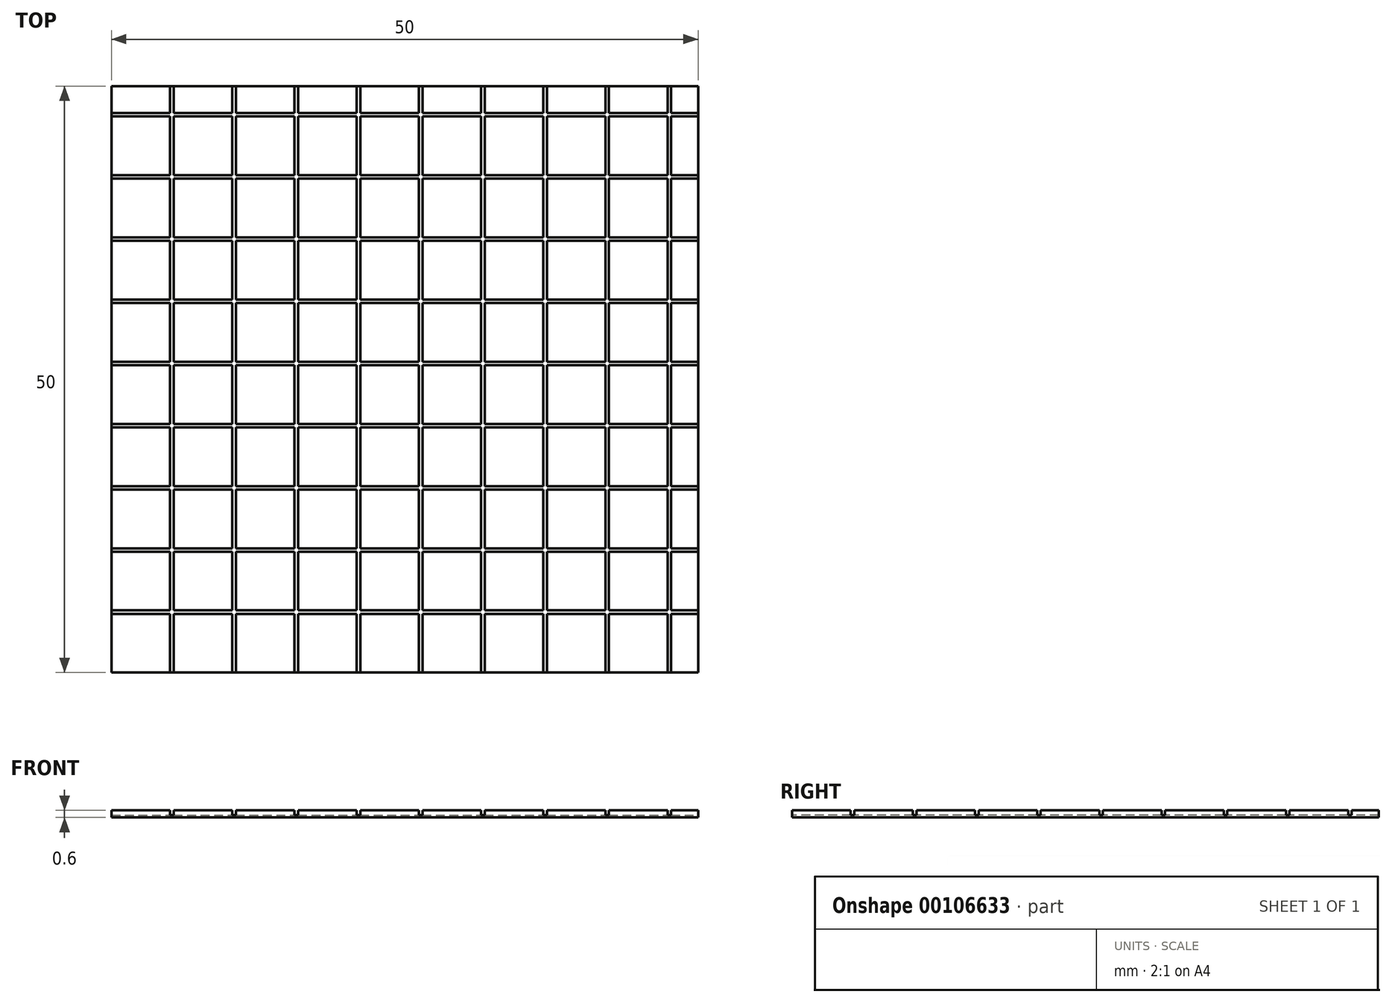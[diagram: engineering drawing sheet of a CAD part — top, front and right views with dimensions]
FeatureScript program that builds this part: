
annotation { "Feature Type Name" : "Feature", "Feature Type Description" : "" }
export const myFeature = defineFeature(function(context is Context, id is Id, definition is map)
    precondition{}
    {
        {
            var Q0;
            Q0=qCreatedBy(makeId("Top.planeOp"),FACE);
            var sketch = newSketch(context, id + "F0", { "sketchPlane" : qUnion([Q0])});
            skLineSegment(sketch, "E0.bottom", {"start": v(0, 0) * mm, "end": v(50, 0) * mm});
            skLineSegment(sketch, "E0.top", {"start": v(0, 50) * mm, "end": v(50, 50) * mm});
            skLineSegment(sketch, "E0.left", {"start": v(0, 0) * mm, "end": v(0, 50) * mm});
            skLineSegment(sketch, "E0.right", {"start": v(50, 0) * mm, "end": v(50, 50) * mm});
            skSolve(sketch);
        }
        {
            var Q0;
            Q0 = qSketchRegion(id + "F0", true);
            extrude(context, id + "F1", {"entities" : qUnion([Q0]), "depth" : 0.6 * mm});
        }
        {
            var Q0;
            Q0=makeQuery(id+"F1.opExtrude","CAP_FACE",FACE,{"disambiguationData":[OSD([sQuery(id+"F0.wireOp",EDGE,"E0.bottom"),sQuery(id+"F0.wireOp",EDGE,"E0.top"),sQuery(id+"F0.wireOp",EDGE,"E0.left"),sQuery(id+"F0.wireOp",EDGE,"E0.right")])],"isStart":false});
            var sketch = newSketch(context, id + "F2", { "sketchPlane" : qUnion([Q0])});
            skLineSegment(sketch, "E1.bottom", {"start": v(5, 50) * mm, "end": v(5.3, 50) * mm});
            skLineSegment(sketch, "E1.top", {"start": v(5, 0) * mm, "end": v(5.3, 0) * mm});
            skLineSegment(sketch, "E1.left", {"start": v(5, 50) * mm, "end": v(5, 0) * mm});
            skLineSegment(sketch, "E1.right", {"start": v(5.3, 50) * mm, "end": v(5.3, 0) * mm});
            skLineSegment(sketch, "E2.1.0.0", {"start": v(10.3, 50) * mm, "end": v(10.3, 0) * mm});
            skLineSegment(sketch, "E2.1.0.1", {"start": v(10.6, 50) * mm, "end": v(10.6, 0) * mm});
            skLineSegment(sketch, "E2.1.0.2", {"start": v(10.3, 0) * mm, "end": v(10.6, 0) * mm});
            skLineSegment(sketch, "E2.1.0.3", {"start": v(10.3, 50) * mm, "end": v(10.6, 50) * mm});
            skLineSegment(sketch, "E2.2.0.0", {"start": v(15.6, 50) * mm, "end": v(15.6, 0) * mm});
            skLineSegment(sketch, "E2.2.0.1", {"start": v(15.9, 50) * mm, "end": v(15.9, 0) * mm});
            skLineSegment(sketch, "E2.2.0.2", {"start": v(15.6, 0) * mm, "end": v(15.9, 0) * mm});
            skLineSegment(sketch, "E2.2.0.3", {"start": v(15.6, 50) * mm, "end": v(15.9, 50) * mm});
            skLineSegment(sketch, "E2.3.0.0", {"start": v(20.9, 50) * mm, "end": v(20.9, 0) * mm});
            skLineSegment(sketch, "E2.3.0.1", {"start": v(21.2, 50) * mm, "end": v(21.2, 0) * mm});
            skLineSegment(sketch, "E2.3.0.2", {"start": v(20.9, 0) * mm, "end": v(21.2, 0) * mm});
            skLineSegment(sketch, "E2.3.0.3", {"start": v(20.9, 50) * mm, "end": v(21.2, 50) * mm});
            skLineSegment(sketch, "E2.4.0.0", {"start": v(26.2, 50) * mm, "end": v(26.2, 0) * mm});
            skLineSegment(sketch, "E2.4.0.1", {"start": v(26.5, 50) * mm, "end": v(26.5, 0) * mm});
            skLineSegment(sketch, "E2.4.0.2", {"start": v(26.2, 0) * mm, "end": v(26.5, 0) * mm});
            skLineSegment(sketch, "E2.4.0.3", {"start": v(26.2, 50) * mm, "end": v(26.5, 50) * mm});
            skLineSegment(sketch, "E2.5.0.0", {"start": v(31.5, 50) * mm, "end": v(31.5, 0) * mm});
            skLineSegment(sketch, "E2.5.0.1", {"start": v(31.8, 50) * mm, "end": v(31.8, 0) * mm});
            skLineSegment(sketch, "E2.5.0.2", {"start": v(31.5, 0) * mm, "end": v(31.8, 0) * mm});
            skLineSegment(sketch, "E2.5.0.3", {"start": v(31.5, 50) * mm, "end": v(31.8, 50) * mm});
            skLineSegment(sketch, "E2.6.0.0", {"start": v(36.8, 50) * mm, "end": v(36.8, 0) * mm});
            skLineSegment(sketch, "E2.6.0.1", {"start": v(37.1, 50) * mm, "end": v(37.1, 0) * mm});
            skLineSegment(sketch, "E2.6.0.2", {"start": v(36.8, 0) * mm, "end": v(37.1, 0) * mm});
            skLineSegment(sketch, "E2.6.0.3", {"start": v(36.8, 50) * mm, "end": v(37.1, 50) * mm});
            skLineSegment(sketch, "E2.7.0.0", {"start": v(42.1, 50) * mm, "end": v(42.1, 0) * mm});
            skLineSegment(sketch, "E2.7.0.1", {"start": v(42.4, 50) * mm, "end": v(42.4, 0) * mm});
            skLineSegment(sketch, "E2.7.0.2", {"start": v(42.1, 0) * mm, "end": v(42.4, 0) * mm});
            skLineSegment(sketch, "E2.7.0.3", {"start": v(42.1, 50) * mm, "end": v(42.4, 50) * mm});
            skLineSegment(sketch, "E2.8.0.0", {"start": v(47.4, 50) * mm, "end": v(47.4, 0) * mm});
            skLineSegment(sketch, "E2.8.0.1", {"start": v(47.7, 50) * mm, "end": v(47.7, 0) * mm});
            skLineSegment(sketch, "E2.8.0.2", {"start": v(47.4, 0) * mm, "end": v(47.7, 0) * mm});
            skLineSegment(sketch, "E2.8.0.3", {"start": v(47.4, 50) * mm, "end": v(47.7, 50) * mm});
            skLineSegment(sketch, "E2.direction1", {"start": v(5, 0) * mm, "end": v(10.3, 0) * mm, "construction": true});
            skSolve(sketch);
        }
        {
            var Q0;
            Q0 = qSketchRegion(id + "F2", true);
            extrude(context, id + "F3", {"entities" : qUnion([Q0]), "oppositeDirection" : true, "depth" : 0.4 * mm});
        }
        {
            var Q0;
            Q0=makeQuery(id+"F1.opExtrude","CAP_FACE",FACE,{"disambiguationData":[OSD([sQuery(id+"F0.wireOp",EDGE,"E0.bottom"),sQuery(id+"F0.wireOp",EDGE,"E0.top"),sQuery(id+"F0.wireOp",EDGE,"E0.left"),sQuery(id+"F0.wireOp",EDGE,"E0.right")])],"isStart":false});
            var sketch = newSketch(context, id + "F4", { "sketchPlane" : qUnion([Q0])});
            skCircle(sketch, "E3", {"center": v(25, 25) * mm, "radius": 8.95 * mm});
            skPoint(sketch, "E3.centerSnap0", {"position": v(50, 25) * mm});
            skPoint(sketch, "E3.centerSnap1", {"position": v(25, 50) * mm});
            skSolve(sketch);
        }
        {
            var Q0;
            Q0=makeQuery(id+"F3.opExtrude","SWEPT_BODY",BODY,{"disambiguationData":[OSD([sQuery(id+"F2.wireOp",EDGE,"E1.bottom"),sQuery(id+"F2.wireOp",EDGE,"E1.top"),sQuery(id+"F2.wireOp",EDGE,"E1.left"),sQuery(id+"F2.wireOp",EDGE,"E1.right")])]});
            var Q1;
            Q1=makeQuery(id+"F3.opExtrude","SWEPT_BODY",BODY,{"disambiguationData":[OSD([sQuery(id+"F2.wireOp",EDGE,"E2.1.0.0"),sQuery(id+"F2.wireOp",EDGE,"E2.1.0.1"),sQuery(id+"F2.wireOp",EDGE,"E2.1.0.2"),sQuery(id+"F2.wireOp",EDGE,"E2.1.0.3")])]});
            var Q2;
            Q2=makeQuery(id+"F3.opExtrude","SWEPT_BODY",BODY,{"disambiguationData":[OSD([sQuery(id+"F2.wireOp",EDGE,"E2.2.0.0"),sQuery(id+"F2.wireOp",EDGE,"E2.2.0.1"),sQuery(id+"F2.wireOp",EDGE,"E2.2.0.2"),sQuery(id+"F2.wireOp",EDGE,"E2.2.0.3")])]});
            var Q3;
            Q3=makeQuery(id+"F3.opExtrude","SWEPT_BODY",BODY,{"disambiguationData":[OSD([sQuery(id+"F2.wireOp",EDGE,"E2.3.0.0"),sQuery(id+"F2.wireOp",EDGE,"E2.3.0.1"),sQuery(id+"F2.wireOp",EDGE,"E2.3.0.2"),sQuery(id+"F2.wireOp",EDGE,"E2.3.0.3")])]});
            var Q4;
            Q4=makeQuery(id+"F3.opExtrude","SWEPT_BODY",BODY,{"disambiguationData":[OSD([sQuery(id+"F2.wireOp",EDGE,"E2.4.0.0"),sQuery(id+"F2.wireOp",EDGE,"E2.4.0.1"),sQuery(id+"F2.wireOp",EDGE,"E2.4.0.2"),sQuery(id+"F2.wireOp",EDGE,"E2.4.0.3")])]});
            var Q5;
            Q5=makeQuery(id+"F3.opExtrude","SWEPT_BODY",BODY,{"disambiguationData":[OSD([sQuery(id+"F2.wireOp",EDGE,"E2.5.0.0"),sQuery(id+"F2.wireOp",EDGE,"E2.5.0.1"),sQuery(id+"F2.wireOp",EDGE,"E2.5.0.2"),sQuery(id+"F2.wireOp",EDGE,"E2.5.0.3")])]});
            var Q6;
            Q6=makeQuery(id+"F3.opExtrude","SWEPT_BODY",BODY,{"disambiguationData":[OSD([sQuery(id+"F2.wireOp",EDGE,"E2.6.0.0"),sQuery(id+"F2.wireOp",EDGE,"E2.6.0.1"),sQuery(id+"F2.wireOp",EDGE,"E2.6.0.2"),sQuery(id+"F2.wireOp",EDGE,"E2.6.0.3")])]});
            var Q7;
            Q7=makeQuery(id+"F3.opExtrude","SWEPT_BODY",BODY,{"disambiguationData":[OSD([sQuery(id+"F2.wireOp",EDGE,"E2.7.0.0"),sQuery(id+"F2.wireOp",EDGE,"E2.7.0.1"),sQuery(id+"F2.wireOp",EDGE,"E2.7.0.2"),sQuery(id+"F2.wireOp",EDGE,"E2.7.0.3")])]});
            var Q8;
            Q8=makeQuery(id+"F3.opExtrude","SWEPT_BODY",BODY,{"disambiguationData":[OSD([sQuery(id+"F2.wireOp",EDGE,"E2.8.0.0"),sQuery(id+"F2.wireOp",EDGE,"E2.8.0.1"),sQuery(id+"F2.wireOp",EDGE,"E2.8.0.2"),sQuery(id+"F2.wireOp",EDGE,"E2.8.0.3")])]});
            var Q9;
            Q9=sQuery(id+"F4.wireOp",EDGE,"E3");
            circularPattern(context, id + "F5", {"entities" : qUnion([Q0, Q1, Q2, Q3, Q4, Q5, Q6, Q7, Q8]), "axis" : qUnion([Q9]), "angle" : 90 * degree, "instanceCount" : 2});
        }
        {
            var Q0;
            Q0=makeQuery(id+"F3.opExtrude","SWEPT_BODY",BODY,{"disambiguationData":[OSD([sQuery(id+"F2.wireOp",EDGE,"E1.bottom"),sQuery(id+"F2.wireOp",EDGE,"E1.top"),sQuery(id+"F2.wireOp",EDGE,"E1.left"),sQuery(id+"F2.wireOp",EDGE,"E1.right")])]});
            var Q1;
            Q1=makeQuery(id+"F5.opPattern","COPY",BODY,{"derivedFrom":makeQuery(id+"F3.opExtrude","SWEPT_BODY",BODY,{"disambiguationData":[OSD([sQuery(id+"F2.wireOp",EDGE,"E1.bottom"),sQuery(id+"F2.wireOp",EDGE,"E1.top"),sQuery(id+"F2.wireOp",EDGE,"E1.left"),sQuery(id+"F2.wireOp",EDGE,"E1.right")])]}),"instanceName":"1"});
            var Q2;
            Q2=makeQuery(id+"F5.opPattern","COPY",BODY,{"derivedFrom":makeQuery(id+"F3.opExtrude","SWEPT_BODY",BODY,{"disambiguationData":[OSD([sQuery(id+"F2.wireOp",EDGE,"E2.1.0.0"),sQuery(id+"F2.wireOp",EDGE,"E2.1.0.1"),sQuery(id+"F2.wireOp",EDGE,"E2.1.0.2"),sQuery(id+"F2.wireOp",EDGE,"E2.1.0.3")])]}),"instanceName":"1"});
            var Q3;
            Q3=makeQuery(id+"F3.opExtrude","SWEPT_BODY",BODY,{"disambiguationData":[OSD([sQuery(id+"F2.wireOp",EDGE,"E2.1.0.0"),sQuery(id+"F2.wireOp",EDGE,"E2.1.0.1"),sQuery(id+"F2.wireOp",EDGE,"E2.1.0.2"),sQuery(id+"F2.wireOp",EDGE,"E2.1.0.3")])]});
            var Q4;
            Q4=makeQuery(id+"F3.opExtrude","SWEPT_BODY",BODY,{"disambiguationData":[OSD([sQuery(id+"F2.wireOp",EDGE,"E2.2.0.0"),sQuery(id+"F2.wireOp",EDGE,"E2.2.0.1"),sQuery(id+"F2.wireOp",EDGE,"E2.2.0.2"),sQuery(id+"F2.wireOp",EDGE,"E2.2.0.3")])]});
            var Q5;
            Q5=makeQuery(id+"F3.opExtrude","SWEPT_BODY",BODY,{"disambiguationData":[OSD([sQuery(id+"F2.wireOp",EDGE,"E2.3.0.0"),sQuery(id+"F2.wireOp",EDGE,"E2.3.0.1"),sQuery(id+"F2.wireOp",EDGE,"E2.3.0.2"),sQuery(id+"F2.wireOp",EDGE,"E2.3.0.3")])]});
            var Q6;
            Q6=makeQuery(id+"F3.opExtrude","SWEPT_BODY",BODY,{"disambiguationData":[OSD([sQuery(id+"F2.wireOp",EDGE,"E2.4.0.0"),sQuery(id+"F2.wireOp",EDGE,"E2.4.0.1"),sQuery(id+"F2.wireOp",EDGE,"E2.4.0.2"),sQuery(id+"F2.wireOp",EDGE,"E2.4.0.3")])]});
            var Q7;
            Q7=makeQuery(id+"F3.opExtrude","SWEPT_BODY",BODY,{"disambiguationData":[OSD([sQuery(id+"F2.wireOp",EDGE,"E2.5.0.0"),sQuery(id+"F2.wireOp",EDGE,"E2.5.0.1"),sQuery(id+"F2.wireOp",EDGE,"E2.5.0.2"),sQuery(id+"F2.wireOp",EDGE,"E2.5.0.3")])]});
            var Q8;
            Q8=makeQuery(id+"F3.opExtrude","SWEPT_BODY",BODY,{"disambiguationData":[OSD([sQuery(id+"F2.wireOp",EDGE,"E2.6.0.0"),sQuery(id+"F2.wireOp",EDGE,"E2.6.0.1"),sQuery(id+"F2.wireOp",EDGE,"E2.6.0.2"),sQuery(id+"F2.wireOp",EDGE,"E2.6.0.3")])]});
            var Q9;
            Q9=makeQuery(id+"F3.opExtrude","SWEPT_BODY",BODY,{"disambiguationData":[OSD([sQuery(id+"F2.wireOp",EDGE,"E2.7.0.0"),sQuery(id+"F2.wireOp",EDGE,"E2.7.0.1"),sQuery(id+"F2.wireOp",EDGE,"E2.7.0.2"),sQuery(id+"F2.wireOp",EDGE,"E2.7.0.3")])]});
            var Q10;
            Q10=makeQuery(id+"F3.opExtrude","SWEPT_BODY",BODY,{"disambiguationData":[OSD([sQuery(id+"F2.wireOp",EDGE,"E2.8.0.0"),sQuery(id+"F2.wireOp",EDGE,"E2.8.0.1"),sQuery(id+"F2.wireOp",EDGE,"E2.8.0.2"),sQuery(id+"F2.wireOp",EDGE,"E2.8.0.3")])]});
            var Q11;
            Q11=makeQuery(id+"F5.opPattern","COPY",BODY,{"derivedFrom":makeQuery(id+"F3.opExtrude","SWEPT_BODY",BODY,{"disambiguationData":[OSD([sQuery(id+"F2.wireOp",EDGE,"E2.2.0.0"),sQuery(id+"F2.wireOp",EDGE,"E2.2.0.1"),sQuery(id+"F2.wireOp",EDGE,"E2.2.0.2"),sQuery(id+"F2.wireOp",EDGE,"E2.2.0.3")])]}),"instanceName":"1"});
            var Q12;
            Q12=makeQuery(id+"F5.opPattern","COPY",BODY,{"derivedFrom":makeQuery(id+"F3.opExtrude","SWEPT_BODY",BODY,{"disambiguationData":[OSD([sQuery(id+"F2.wireOp",EDGE,"E2.3.0.0"),sQuery(id+"F2.wireOp",EDGE,"E2.3.0.1"),sQuery(id+"F2.wireOp",EDGE,"E2.3.0.2"),sQuery(id+"F2.wireOp",EDGE,"E2.3.0.3")])]}),"instanceName":"1"});
            var Q13;
            Q13=makeQuery(id+"F5.opPattern","COPY",BODY,{"derivedFrom":makeQuery(id+"F3.opExtrude","SWEPT_BODY",BODY,{"disambiguationData":[OSD([sQuery(id+"F2.wireOp",EDGE,"E2.4.0.0"),sQuery(id+"F2.wireOp",EDGE,"E2.4.0.1"),sQuery(id+"F2.wireOp",EDGE,"E2.4.0.2"),sQuery(id+"F2.wireOp",EDGE,"E2.4.0.3")])]}),"instanceName":"1"});
            var Q14;
            Q14=makeQuery(id+"F5.opPattern","COPY",BODY,{"derivedFrom":makeQuery(id+"F3.opExtrude","SWEPT_BODY",BODY,{"disambiguationData":[OSD([sQuery(id+"F2.wireOp",EDGE,"E2.5.0.0"),sQuery(id+"F2.wireOp",EDGE,"E2.5.0.1"),sQuery(id+"F2.wireOp",EDGE,"E2.5.0.2"),sQuery(id+"F2.wireOp",EDGE,"E2.5.0.3")])]}),"instanceName":"1"});
            var Q15;
            Q15=makeQuery(id+"F5.opPattern","COPY",BODY,{"derivedFrom":makeQuery(id+"F3.opExtrude","SWEPT_BODY",BODY,{"disambiguationData":[OSD([sQuery(id+"F2.wireOp",EDGE,"E2.6.0.0"),sQuery(id+"F2.wireOp",EDGE,"E2.6.0.1"),sQuery(id+"F2.wireOp",EDGE,"E2.6.0.2"),sQuery(id+"F2.wireOp",EDGE,"E2.6.0.3")])]}),"instanceName":"1"});
            var Q16;
            Q16=makeQuery(id+"F5.opPattern","COPY",BODY,{"derivedFrom":makeQuery(id+"F3.opExtrude","SWEPT_BODY",BODY,{"disambiguationData":[OSD([sQuery(id+"F2.wireOp",EDGE,"E2.7.0.0"),sQuery(id+"F2.wireOp",EDGE,"E2.7.0.1"),sQuery(id+"F2.wireOp",EDGE,"E2.7.0.2"),sQuery(id+"F2.wireOp",EDGE,"E2.7.0.3")])]}),"instanceName":"1"});
            var Q17;
            Q17=makeQuery(id+"F5.opPattern","COPY",BODY,{"derivedFrom":makeQuery(id+"F3.opExtrude","SWEPT_BODY",BODY,{"disambiguationData":[OSD([sQuery(id+"F2.wireOp",EDGE,"E2.8.0.0"),sQuery(id+"F2.wireOp",EDGE,"E2.8.0.1"),sQuery(id+"F2.wireOp",EDGE,"E2.8.0.2"),sQuery(id+"F2.wireOp",EDGE,"E2.8.0.3")])]}),"instanceName":"1"});
            var Q18;
            Q18=makeQuery(id+"F1.opExtrude","SWEPT_BODY",BODY,{"disambiguationData":[OSD([sQuery(id+"F0.wireOp",EDGE,"E0.bottom"),sQuery(id+"F0.wireOp",EDGE,"E0.top"),sQuery(id+"F0.wireOp",EDGE,"E0.left"),sQuery(id+"F0.wireOp",EDGE,"E0.right")])]});
            booleanBodies(context, id + "F6", {"operationType" : BooleanOperationType.SUBTRACTION, "tools" : qUnion([Q0, Q1, Q2, Q3, Q4, Q5, Q6, Q7, Q8, Q9, Q10, Q11, Q12, Q13, Q14, Q15, Q16, Q17]), "targets" : qUnion([Q18])});
        }
    });
